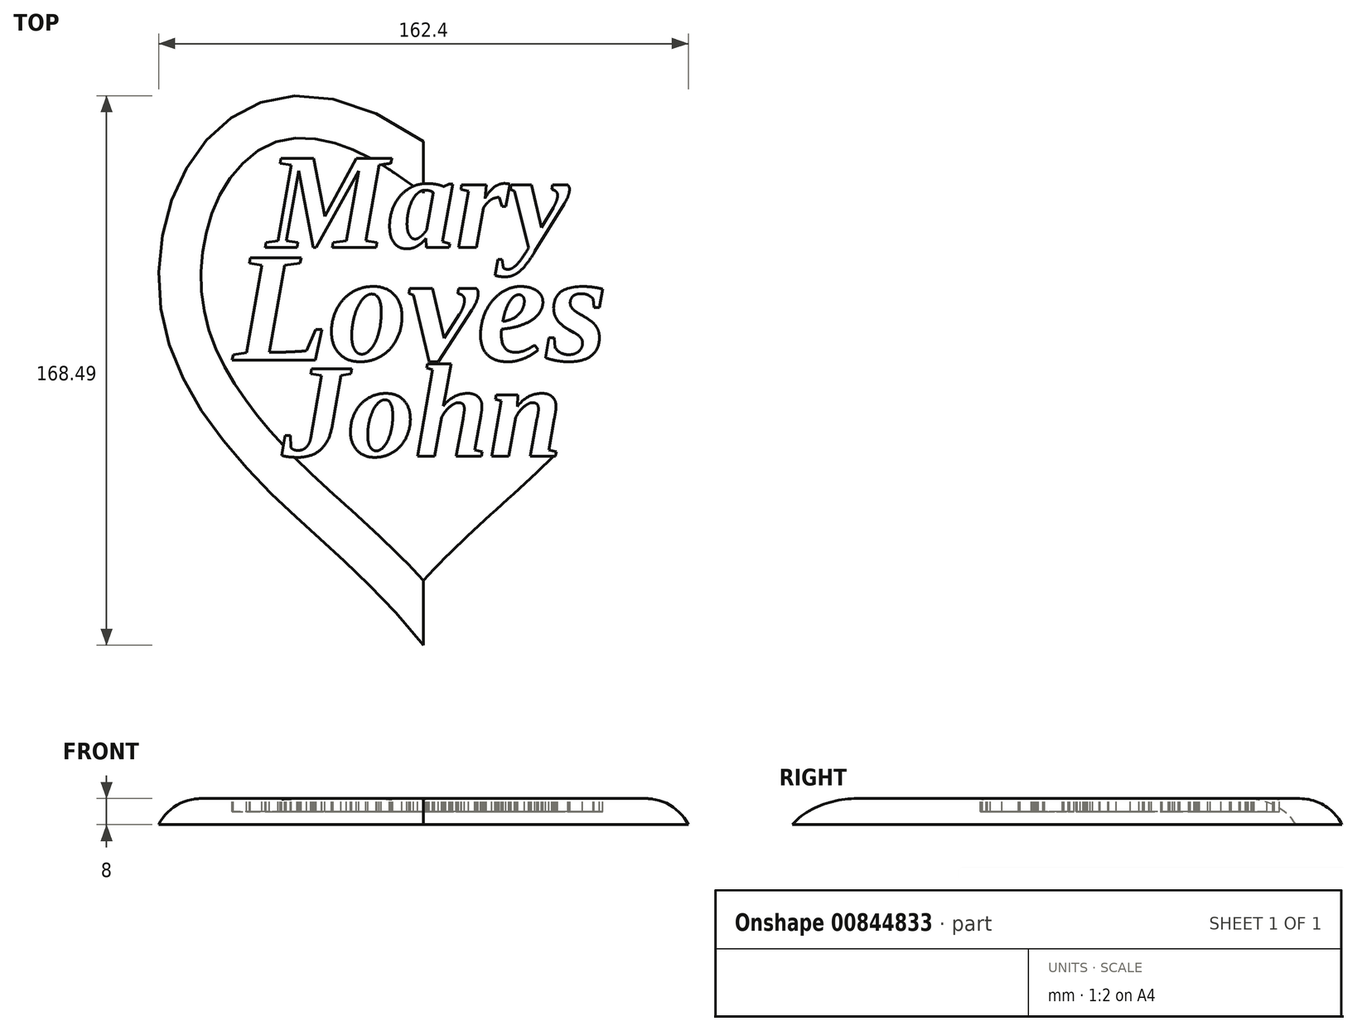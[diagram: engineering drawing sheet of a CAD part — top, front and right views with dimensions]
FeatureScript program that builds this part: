
annotation { "Feature Type Name" : "Feature", "Feature Type Description" : "" }
export const myFeature = defineFeature(function(context is Context, id is Id, definition is map)
    precondition{}
    {
        {
            var Q0;
            Q0=qCreatedBy(makeId("Top.planeOp"),FACE);
            var sketch = newSketch(context, id + "F0", { "sketchPlane" : qUnion([Q0])});
            skFitSpline(sketch, "E0", {"points": [v(0, 77.5) * mm, v(-65.7, 78.89) * mm, v(-79.58, 21.26) * mm, v(-44.87, -32.2) * mm, v(0, -76.92) * mm], "startDerivative": vector(-347.72, 244.75) * mm, "endDerivative": vector(204.69, -252.63) * mm});
            skFitSpline(sketch, "E1.MirrorCS", {"points": [v(0, 77.5) * mm, v(65.7, 78.89) * mm, v(79.58, 21.26) * mm, v(44.87, -32.2) * mm, v(0, -76.92) * mm], "startDerivative": vector(347.72, 244.75) * mm, "endDerivative": vector(-204.69, -252.63) * mm});
            skSolve(sketch);
        }
        {
            var Q0;
            Q0=makeQuery(id+"F0.imprint","IMPRINT",FACE,{"disambiguationData":[TD([[makeQuery(id+"F0.imprint","IMPRINT",EDGE,{"derivedFrom":sQuery(id+"F0.wireOp",EDGE,"E0")}),1.0]])]});
            extrude(context, id + "F1", {"entities" : qUnion([Q0]), "depth" : 8 * mm, "offsetDistance" : 25 * mm});
        }
        {
            var Q0;
            Q0=makeQuery(id+"F1.opExtrude","CAP_EDGE",EDGE,{"disambiguationData":[OSD([sQuery(id+"F0.wireOp",EDGE,"E0")])],"isStart":false});
            var Q1;
            Q1=makeQuery(id+"F1.opExtrude","CAP_EDGE",EDGE,{"disambiguationData":[OSD([sQuery(id+"F0.wireOp",EDGE,"E1.MirrorCS")])],"isStart":false});
            fillet(context, id + "F2", {"entities" : qUnion([Q0, Q1]), "radius" : 14.5 * mm, "tangentPropagation" : true, "allowEdgeOverflow" : false});
        }
        {
            var Q0;
            Q0=makeQuery(id+"F1.opExtrude","CAP_FACE",FACE,{"disambiguationData":[OSD([sQuery(id+"F0.wireOp",EDGE,"E0"),sQuery(id+"F0.wireOp",EDGE,"E1.MirrorCS")])],"isStart":false});
            var sketch = newSketch(context, id + "F3", { "sketchPlane" : qUnion([Q0])});
            skText(sketch, "E2", { "text": "Mary", "fontName": "Tinos-BoldItalic.ttf"});
            skText(sketch, "E3", { "text": "Loves", "fontName": "Tinos-BoldItalic.ttf"});
            skText(sketch, "E4", { "text": "John", "fontName": "Tinos-BoldItalic.ttf"});
            const initialGuessF3  = {"E2": [-0.04793, 0.04503, 1, 0, 0.03], "E3": [-0.05829, 0.01045, 1, 0, 0.03458], "E4": [-0.0434, -0.01891, 1, 0, 0.02936]};
            skSetInitialGuess(sketch, initialGuessF3);
            skSolve(sketch);
        }
        {
            var Q0;
            Q0 = qSketchRegion(id + "F3", true);
            extrude(context, id + "F4", {"entities" : qUnion([Q0]), "operationType" : NewBodyOperationType.REMOVE, "oppositeDirection" : true, "depth" : 4 * mm, "offsetDistance" : 25 * mm});
        }
    });
